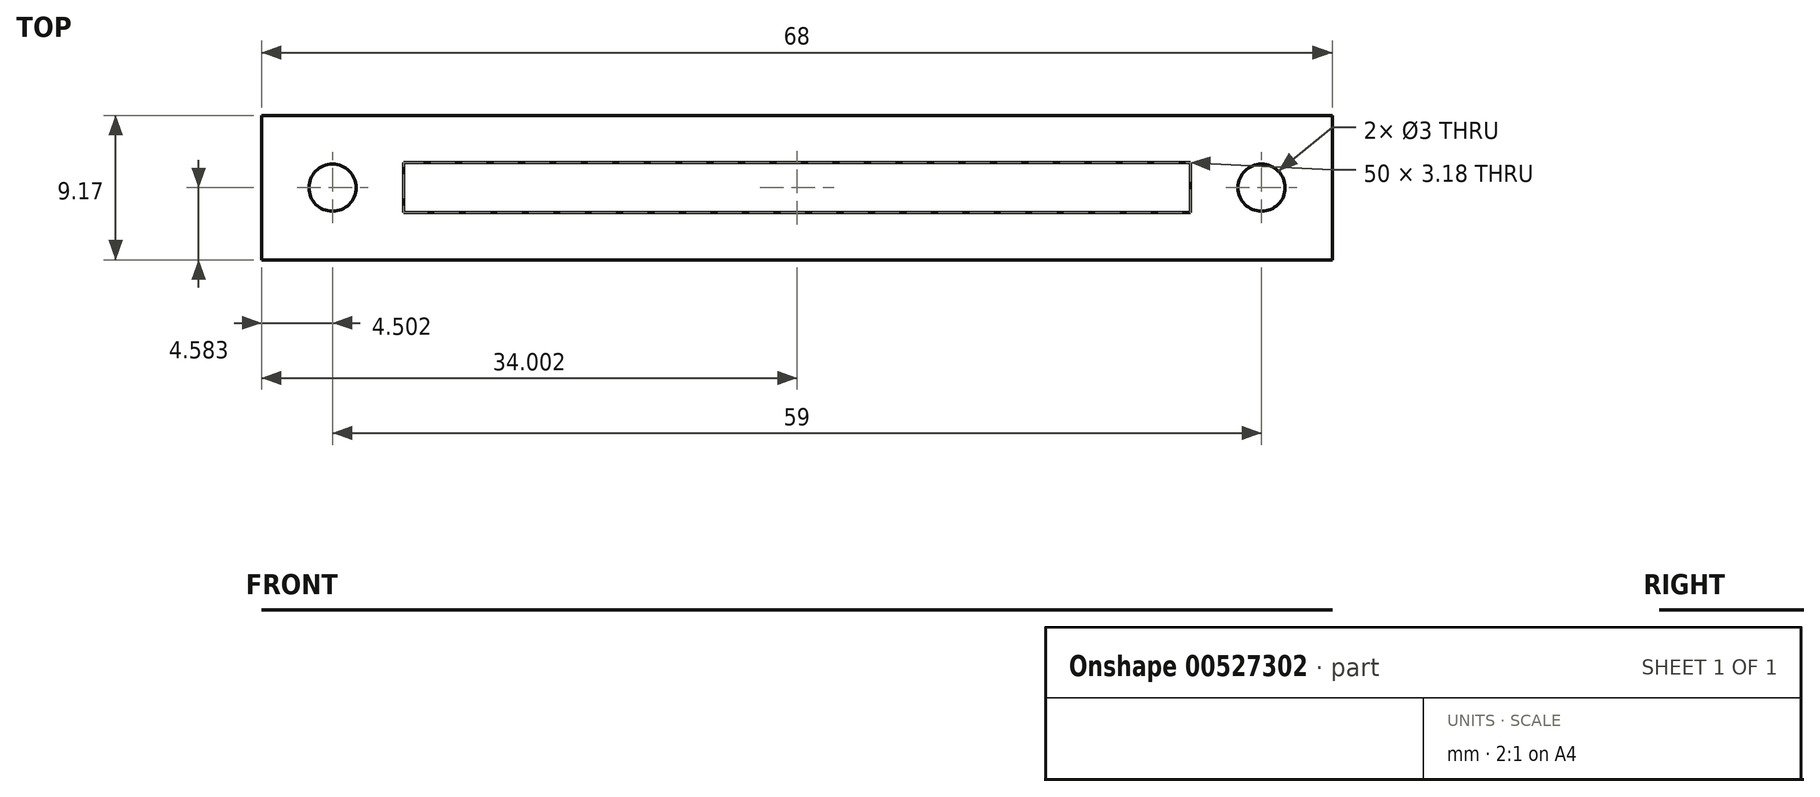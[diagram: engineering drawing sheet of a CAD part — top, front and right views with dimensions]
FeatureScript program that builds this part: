
annotation { "Feature Type Name" : "Feature", "Feature Type Description" : "" }
export const myFeature = defineFeature(function(context is Context, id is Id, definition is map)
    precondition{}
    {
        {
            var Q0;
            Q0=qCreatedBy(makeId("Top.planeOp"),FACE);
            var sketch = newSketch(context, id + "F0", { "sketchPlane" : qUnion([Q0])});
            skLineSegment(sketch, "E0.bottom", {"start": v(3.92, 18.22) * mm, "end": v(53.92, 18.22) * mm});
            skLineSegment(sketch, "E0.top", {"start": v(3.92, 15.05) * mm, "end": v(53.92, 15.05) * mm});
            skLineSegment(sketch, "E0.left", {"start": v(3.92, 18.22) * mm, "end": v(3.92, 15.05) * mm});
            skLineSegment(sketch, "E0.right", {"start": v(53.92, 18.22) * mm, "end": v(53.92, 15.05) * mm});
            skPoint(sketch, "E0.middle", {"position": v(28.92, 16.63) * mm});
            skCircle(sketch, "E1", {"center": v(-0.58, 16.63) * mm, "radius": 1.5 * mm});
            skLineSegment(sketch, "E2", {"start": v(28.92, 16.63) * mm, "end": v(28.92, 18.22) * mm});
            skCircle(sketch, "E3.MirrorC", {"center": v(58.42, 16.63) * mm, "radius": 1.5 * mm});
            skLineSegment(sketch, "E4.bottom", {"start": v(-5.08, 12.05) * mm, "end": v(62.92, 12.05) * mm});
            skLineSegment(sketch, "E4.top", {"start": v(-5.08, 21.22) * mm, "end": v(62.92, 21.22) * mm});
            skLineSegment(sketch, "E4.left", {"start": v(-5.08, 12.05) * mm, "end": v(-5.08, 21.22) * mm});
            skLineSegment(sketch, "E4.right", {"start": v(62.92, 12.05) * mm, "end": v(62.92, 21.22) * mm});
            skSolve(sketch);
        }
        {
            var Q0;
            Q0=makeQuery(id+"F0.imprint","IMPRINT",FACE,{"disambiguationData":[TD([[makeQuery(id+"F0.imprint","IMPRINT",EDGE,{"derivedFrom":sQuery(id+"F0.wireOp",EDGE,"E0.top")}),-1.0]])]});
            extrude(context, id + "F1", {"entities" : qUnion([Q0]), "depth" : 1 / 203.2 * mm, "offsetDistance" : 25 * mm});
        }
    });
